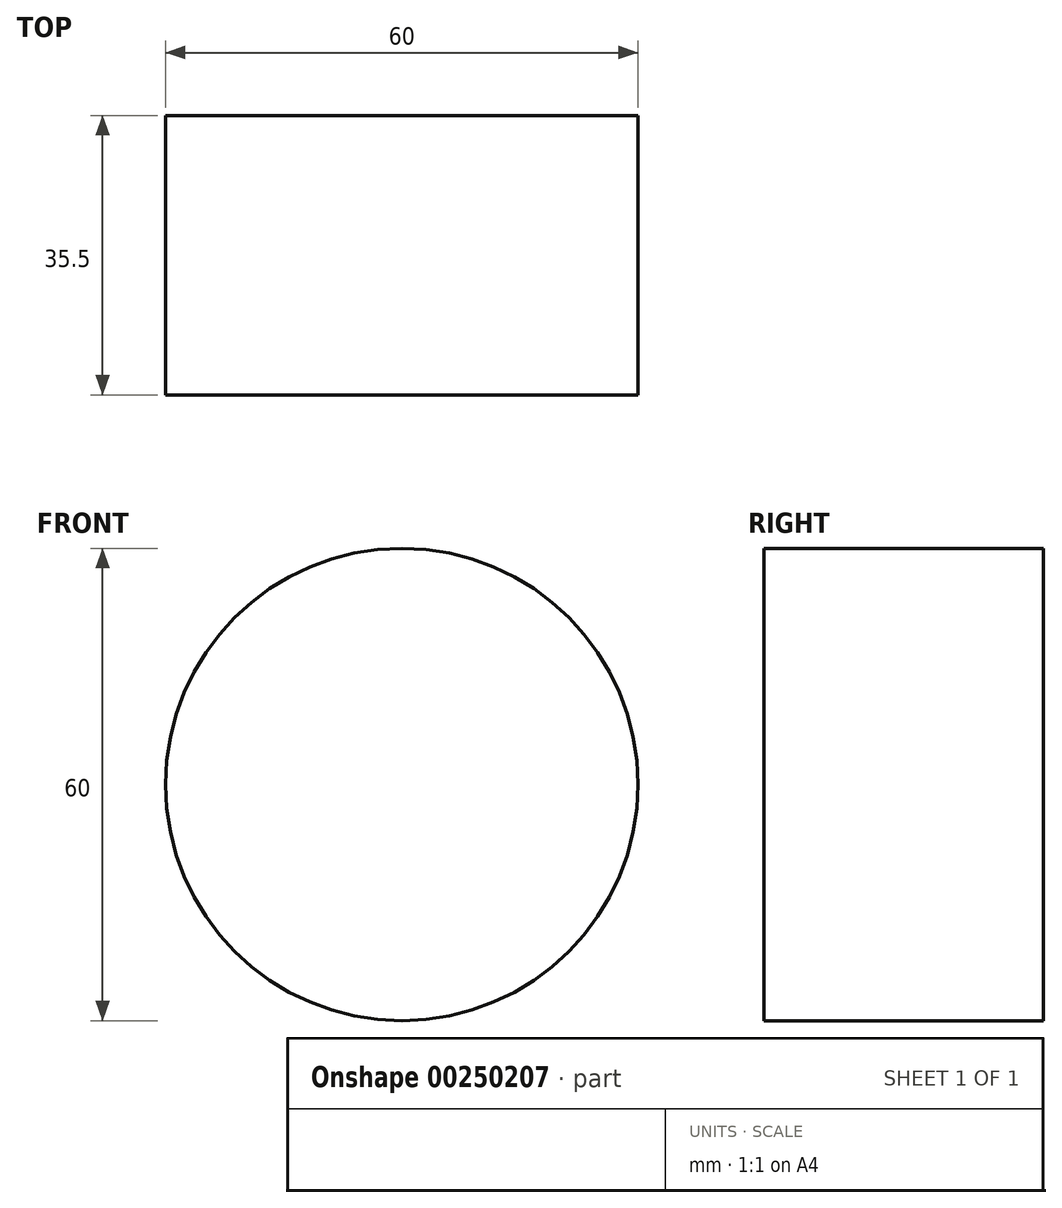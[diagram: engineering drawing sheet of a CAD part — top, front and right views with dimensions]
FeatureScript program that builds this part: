
annotation { "Feature Type Name" : "Feature", "Feature Type Description" : "" }
export const myFeature = defineFeature(function(context is Context, id is Id, definition is map)
    precondition{}
    {
        {
            var Q0;
            Q0=qCreatedBy(makeId("Front.planeOp"),FACE);
            var sketch = newSketch(context, id + "F0", { "sketchPlane" : qUnion([Q0])});
            skCircle(sketch, "E0", {"center": v(0, 0) * mm, "radius": 30 * mm});
            skSolve(sketch);
        }
        {
            var Q0;
            Q0 = qSketchRegion(id + "F0", true);
            extrude(context, id + "F1", {"entities" : qUnion([Q0]), "depth" : 35.5 * mm});
        }
    });
